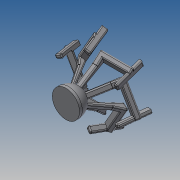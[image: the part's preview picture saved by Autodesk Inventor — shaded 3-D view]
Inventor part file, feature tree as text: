
AUTODESK INVENTOR PART (.ipt)
format: ipt  version: 2015 (Build 190159000, 159)  size: 551,936 bytes
history: native  units: mm
features: sketch x4, extrude x3, projected_geometry x2, revolve x1, fillet x1, pattern_circular x1
ambient origin geometry x8: Origin, YZ Plane, XZ Plane, XY Plane, X Axis, Y Axis, Z Axis, Center Point
bodies: Solid1 (feature_tree)
feature tree (12):
  revolve  "Revolution1"  [1 undecoded]
  extrude  "Extrusion1"  Depth=10.0mm TaperAngle=0.0deg
  extrude  "Extrusion2"  Depth=50.0mm TaperAngle=0.0deg
  extrude  "Extrusion3"  Depth=2.0mm
  fillet  "Fillet1"  [1 undecoded]
  pattern_circular  "Circular Pattern1"  [2 undecoded]
  sketch  "Sketch1"  dims[d0=30.0mm d1=50.0mm]
  sketch  "Sketch2"  dims[d3=90.0deg d4=10.0mm d5=0.0mm]
  sketch  "Sketch3"  dims[d6=50.0mm d7=0.0mm d8=50.0mm d9=0.0mm]
  projected_geometry  "Projected Loop1"
  sketch  "Sketch4"  dims[d10=60.0mm d11=360.0deg d14=2.0mm]
  projected_geometry  "Projected Loop2"
note: 4 required parameter values undecoded (feature->parameter linkage not recoverable at this tier; creation-order binding heuristic only, values carry confidence <= 0.55)